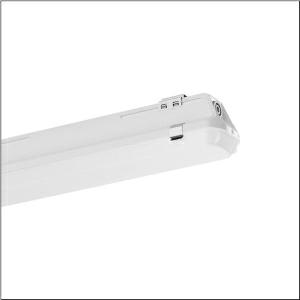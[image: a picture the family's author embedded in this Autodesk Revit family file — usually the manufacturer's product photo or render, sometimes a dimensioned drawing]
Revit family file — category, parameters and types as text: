
# Revit family: monsun_11_51fp20dp4b0u
name_source: partatom
category: Lighting Fixtures
units: mm (PartAtom-declared; Revit-internal decimal feet)

## family parameters
Cut with Voids When Loaded = No
Host = Face
Light Source = No
Part Type = Normal
Room Calculation Point = No
Round Connector Dimension = Use Diameter
Shared = No

## types (1)
- --- (1 x LED, 10950 lm, 63.7 W, 4000K)
    Apparent Load = 64 VA
    CIE Flux Codes = 45 75 93 94 100
    Color Rendering = 80
    Color Temperature = 4000K
    Default Elevation = 1800 mm
    Description = Monsun 11, damp-proof luminaire, chain hanger, primary optical cover: enclosure, of PC, light emission: direct distribution, primary light characteristic: symmetric, installation type: suspended mounting, surface-mounted, horizontal mounting, vertical mounting, LED, rated luminous flux: 10.950lm, luminous efficacy: 172lm/W, light colour: 840, colour temperature: 4000K, control gear: DALI 2, with terminal, 5-pole, max. 2.5mm², mains connection: 220..240V, AC, 50/60Hz, rated input power: 64W, luminaire housing, of glass-fibre reinforced polyester, uncoated, bright grey, incl. chain hanger, length: 1.590mm, width: 90mm, height: 88mm, clip for enclosure, of stainless steel (V2A), ceiling mounting element, of stainless steel (V2A), chain hanger, of stainless steel (V2A), protection rating (complete): IP66, insulation class (complete): insulation class I (protective earthing), certification: CE, ENEC, VDE, UKCA, protection symbol: D, impact resistance: IK08, permissible operating ambient temperature: -40..+35°C, standard: EN 50419, EN 60598-2-1, contact your sales advisor before using the luminaires in applications with unclear chemical exposure, large temperature fluctuations or condensation-forming humidity, LABS conformity tested according to VDMA 24364:2018-05, no direct snow, no direct sun, no direct rain, for indoor or canopied outdoor use, corresponds to IFS (International Featured Standards) requirements for safety and quality in the food industry, packaging unit: 1 piece
    Height = 89 mm
    Lamp = 1 x LED
    Lamp Light Flux = 10950 lm
    Lamp Power = 63.7 W
    Lamp count = 1
    Length = 1590 mm
    Luminous efficacy = 172 lm/W
    Manufacturer = Siteco
    ModVariant = No
    Model = 51FP20DP4B0U
    Mounting Place = Ceiling
    Mounting Type = Surface mounted
    Number of Poles = 1
    OnlyDefault = Yes
    Power Factor = 1
    Product Name = Monsun 11
    Product group = damp-proof luminaire
    ProductGroupID = 300
    Protection Class = Protection class I
    Protection Degree = IP 66
    RLX_Detail_Level = 1
    RLX_Emergency_Light_Flux = 0 lm
    RLX_Emergency_Type = 0
    RLX_Emergency_Type_DB = No
    RlxData = <blob elided: 91929 chars, md5=034aca36>
    Socket = socket
    Standby Power = 0 W
    System Light Flux = 10950 lm
    System Power = 64 W
    Type Comments = factory setting: luminous flux: 100 % | dim-lin: 254 | 441 mA
    Type Image = l_1349237.jpg
    URL = http://relux.com
    VarID = @adj_039367
    Voltage = 0 V
    Weight = 0.00 kg
    Width = 90 mm

## geometry (parser evidence)
native form markers: Blend x4, Sweep x15
no freeform markers — native parametric forms only
